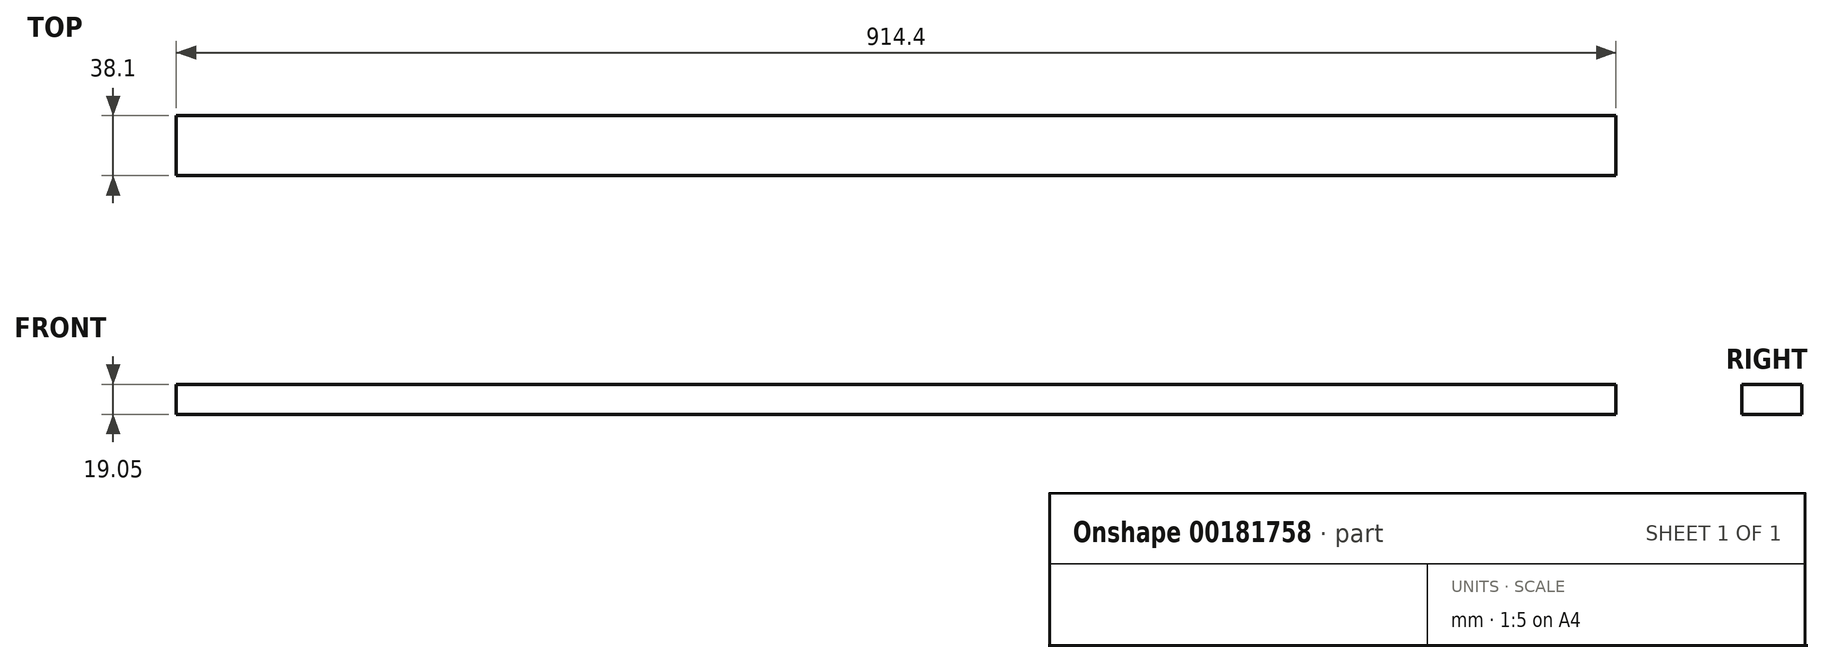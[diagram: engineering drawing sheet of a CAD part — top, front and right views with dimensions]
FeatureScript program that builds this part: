
annotation { "Feature Type Name" : "Feature", "Feature Type Description" : "" }
export const myFeature = defineFeature(function(context is Context, id is Id, definition is map)
    precondition{}
    {
        {
            var Q0;
            Q0=qCreatedBy(makeId("Top.planeOp"),FACE);
            var sketch = newSketch(context, id + "F0", { "sketchPlane" : qUnion([Q0])});
            skLineSegment(sketch, "E0.bottom", {"start": v(-170.58, 0) * mm, "end": v(743.82, 0) * mm});
            skLineSegment(sketch, "E0.top", {"start": v(-170.58, 38.1) * mm, "end": v(743.82, 38.1) * mm});
            skLineSegment(sketch, "E0.left", {"start": v(-170.58, 0) * mm, "end": v(-170.58, 38.1) * mm});
            skLineSegment(sketch, "E0.right", {"start": v(743.82, 0) * mm, "end": v(743.82, 38.1) * mm});
            skSolve(sketch);
        }
        {
            var Q0;
            Q0 = qSketchRegion(id + "F0", true);
            extrude(context, id + "F1", {"entities" : qUnion([Q0]), "depth" : 19.05 * mm});
        }
    });
